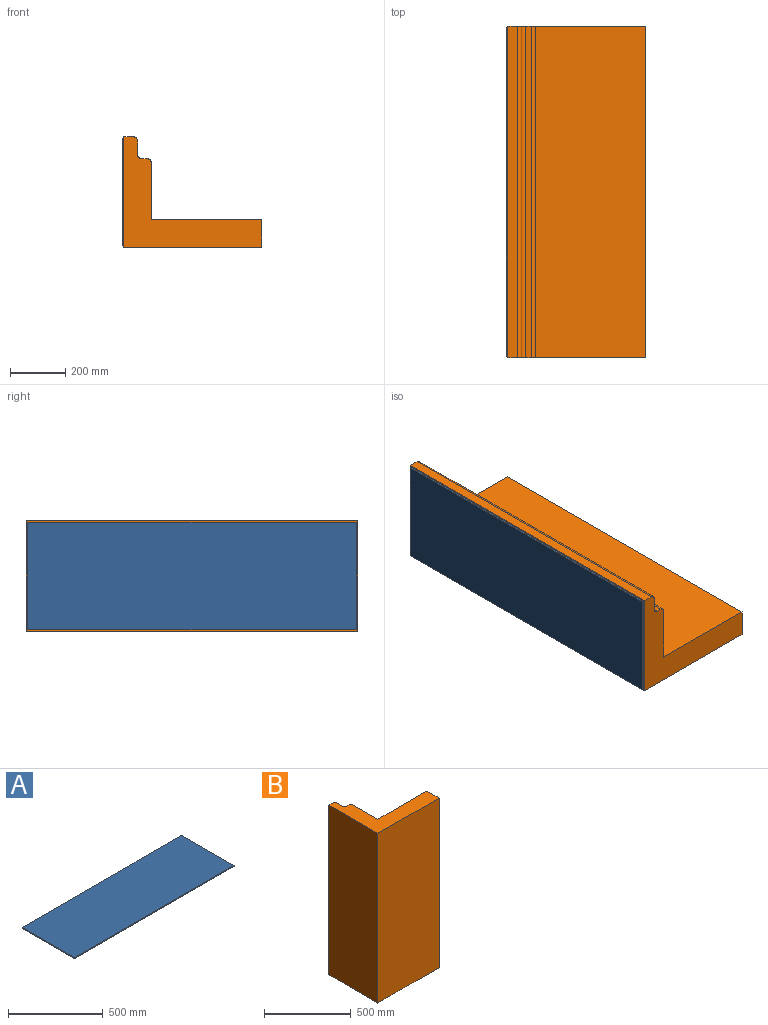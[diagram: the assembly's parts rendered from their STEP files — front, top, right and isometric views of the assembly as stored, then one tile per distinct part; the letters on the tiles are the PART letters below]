
ASSEMBLY  parts=2 mates=1
PART A: 6 faces, bbox 1190x390x6 mm
  f0: plane 1190x6mm, normal (0,1,0), area 7140mm2, adj f1,f3,f4,f5
  f1: plane 390x6mm, normal (-1,0,0), area 2340mm2, adj f0,f2,f4,f5
  f2: plane 1190x6mm, normal (0,-1,0), area 7140mm2, adj f1,f3,f4,f5
  f3: plane 390x6mm, normal (1,0,0), area 2340mm2, adj f0,f2,f4,f5
  f4: plane 1190x390mm, normal (0,0,1), area 464100mm2, adj f0,f1,f2,f3
  f5: plane 1190x390mm, normal (0,0,-1), area 464100mm2, adj f0,f1,f2,f3
PART B: 13 faces, bbox 500x400x1200 mm
  f0: plane 1200x500mm, normal (0,-1,0), area 600000mm2, adj f1,f7,f8,f9
  f1: plane 1200x100mm, normal (1,0,0), area 120000mm2, adj f0,f2,f8,f9
  f2: plane 1200x400mm, normal (0,1,0), area 480000mm2, adj f1,f3,f8,f9
  f3: plane 1200x205mm, normal (1,0,0), area 246000mm2, adj f2,f8,f9,f10
  f4: plane 1200x20mm, normal (0,1,0), area 24000mm2, adj f8,f9,f10,f12
  f5: plane 1200x50mm, normal (1,0,0), area 60000mm2, adj f8,f9,f11,f12
  f6: plane 1200x35mm, normal (0,1,0), area 42000mm2, adj f7,f8,f9,f11
  f7: plane 1200x400mm, normal (-1,0,0), area 480000mm2, adj f0,f6,f8,f9
  f8: plane 500x400mm, normal (0,0,1), area 75951.7mm2, adj f0,f1,f2,f3,f4,f5,f6,f7
  f9: plane 500x400mm, normal (0,0,-1), area 75951.7mm2, adj f0,f1,f2,f3,f4,f5,f6,f7
  f10: cylinder r=15mm len=1200mm, axis (0,0,-1), area 28274.3mm2, adj f3,f4,f8,f9
  f11: cylinder r=15mm len=1200mm, axis (0,0,-1), area 28274.3mm2, adj f5,f6,f8,f9
  f12: cylinder r=15mm len=1200mm, axis (0,0,1), area 28274.3mm2, adj f4,f5,f8,f9
PLACE A rot(axis=(0.58,-0.58,-0.58),120deg) t=(-2409.91,770.91,201.82)mm
PLACE B rot(axis=(1,0,0),90deg) t=(-1909.91,1370.91,1.82)mm
MATE parallel B.f7 <-> A.f5  axis (-1,0,0) through (-2409.91,770.91,201.82)mm
